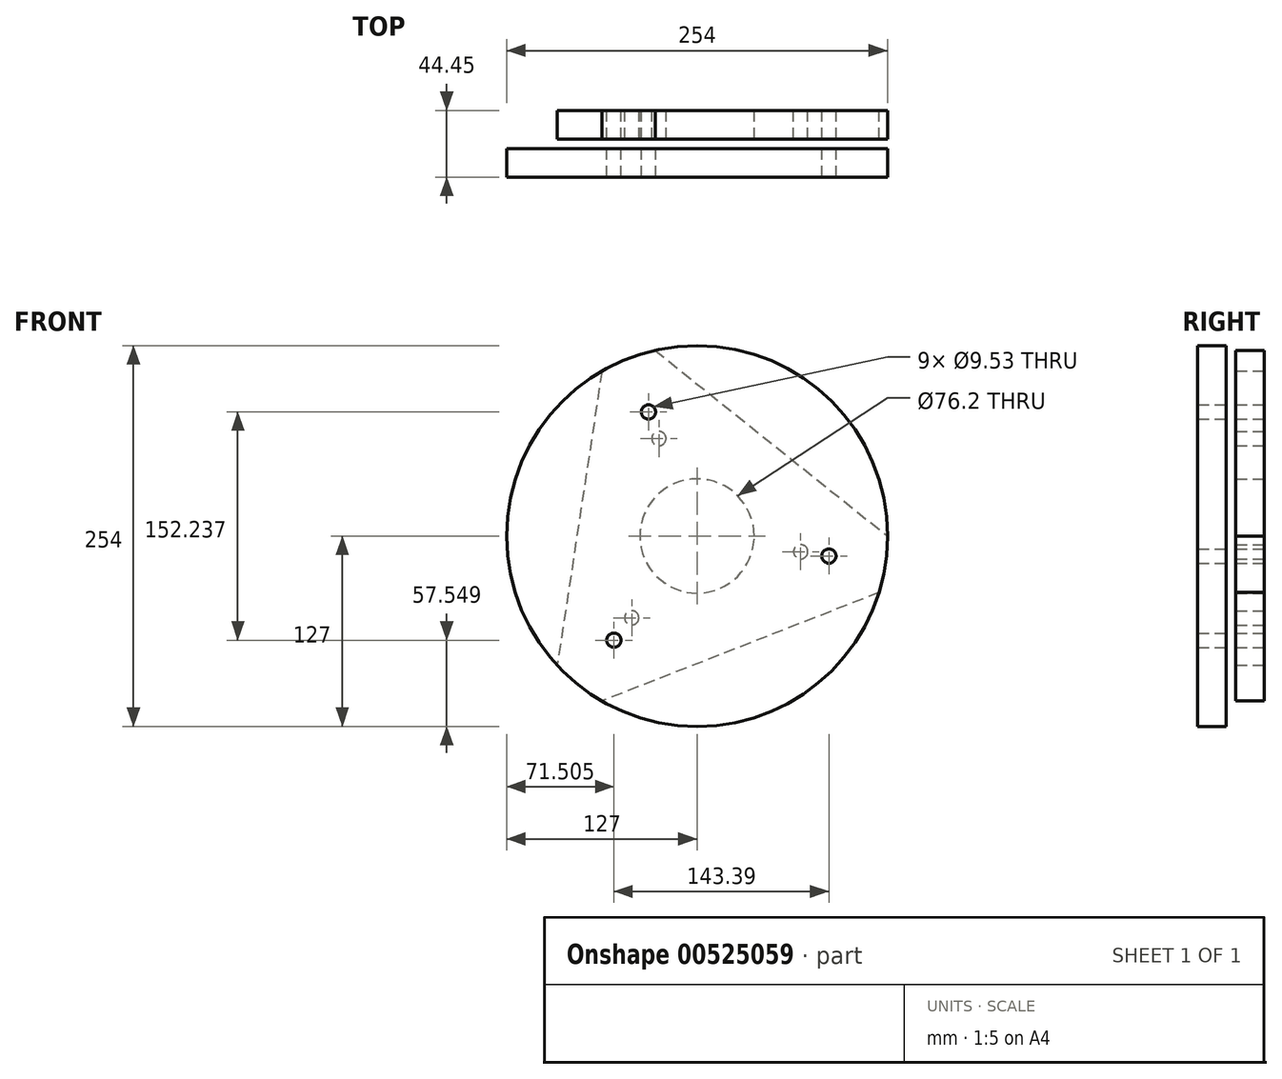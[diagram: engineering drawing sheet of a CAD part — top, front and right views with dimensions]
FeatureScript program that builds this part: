
annotation { "Feature Type Name" : "Feature", "Feature Type Description" : "" }
export const myFeature = defineFeature(function(context is Context, id is Id, definition is map)
    precondition{}
    {
        {
            var Q0;
            Q0=qCreatedBy(makeId("Front.planeOp"),FACE);
            var sketch = newSketch(context, id + "F0", { "sketchPlane" : qUnion([Q0])});
            skArc(sketch, "E0", {"start": v(-93.26, -86.2) * mm, "mid": v(-79.28, -99.22) * mm, "end": v(-63.5, -109.99) * mm});
            skCircle(sketch, "E1", {"center": v(0, 0) * mm, "radius": 38.1 * mm});
            skLineSegment(sketch, "E2", {"start": v(-63.5, 109.99) * mm, "end": v(-93.26, -86.2) * mm});
            skLineSegment(sketch, "E3", {"start": v(-28.02, 123.87) * mm, "end": v(127, 0) * mm});
            skLineSegment(sketch, "E4", {"start": v(121.29, -37.67) * mm, "end": v(-63.5, -109.99) * mm});
            skArc(sketch, "E5.trimOffspring", {"start": v(-28.02, 123.87) * mm, "mid": v(-46.28, 118.27) * mm, "end": v(-63.5, 109.99) * mm});
            skArc(sketch, "E6.trimOffspring", {"start": v(121.28, -37.67) * mm, "mid": v(125.56, -19.05) * mm, "end": v(127, 0) * mm});
            skLineSegment(sketch, "E7", {"start": v(0, 0) * mm, "end": v(-79.28, -99.22) * mm, "construction": true});
            skCircle(sketch, "E8", {"center": v(-55.5, -69.45) * mm, "radius": 4.76 * mm});
            skCircle(sketch, "E9", {"center": v(-43.6, -54.57) * mm, "radius": 4.76 * mm});
            skCircle(sketch, "E10.1.0", {"center": v(69.06, -10.48) * mm, "radius": 4.76 * mm});
            skCircle(sketch, "E10.1.1", {"center": v(87.9, -13.33) * mm, "radius": 4.76 * mm});
            skCircle(sketch, "E10.2.0", {"center": v(-25.46, 65.05) * mm, "radius": 4.76 * mm});
            skCircle(sketch, "E10.2.1", {"center": v(-32.4, 82.79) * mm, "radius": 4.76 * mm});
            skSolve(sketch);
        }
        {
            var Q0;
            Q0=makeQuery(id+"F0.imprint","IMPRINT",FACE,{"disambiguationData":[TD([[makeQuery(id+"F0.imprint","IMPRINT",EDGE,{"derivedFrom":sQuery(id+"F0.wireOp",EDGE,"E0")}),1.0]])]});
            extrude(context, id + "F1", {"entities" : qUnion([Q0]), "depth" : 19.05 * mm, "offsetDistance" : 25.4 * mm});
        }
        {
            var Q0;
            Q0=qCreatedBy(makeId("Front.planeOp"),FACE);
            cPlane(context, id + "F2", {"entities" : qUnion([Q0]), "cplaneType" : CPlaneType.OFFSET, "offset" : 25.4 * mm, "width" : 152.4 * mm, "height" : 152.4 * mm});
        }
        {
            var Q0;
            Q0=qCreatedBy(id+"F2.planeOp",FACE);
            var sketch = newSketch(context, id + "F3", { "sketchPlane" : qUnion([Q0])});
            skCircle(sketch, "E11", {"center": v(0, 0) * mm, "radius": 127 * mm});
            skCircle(sketch, "E12", {"center": v(-55.5, -69.45) * mm, "radius": 4.76 * mm});
            skCircle(sketch, "E13", {"center": v(87.9, -13.33) * mm, "radius": 4.76 * mm});
            skCircle(sketch, "E14", {"center": v(-32.4, 82.79) * mm, "radius": 4.76 * mm});
            skSolve(sketch);
        }
        {
            var Q0;
            Q0=makeQuery(id+"F3.imprint","IMPRINT",FACE,{"disambiguationData":[TD([[makeQuery(id+"F3.imprint","IMPRINT",EDGE,{"derivedFrom":sQuery(id+"F3.wireOp",EDGE,"E11")}),1.0]])]});
            extrude(context, id + "F4", {"entities" : qUnion([Q0]), "depth" : 19.05 * mm, "offsetDistance" : 25.4 * mm});
        }
    });
